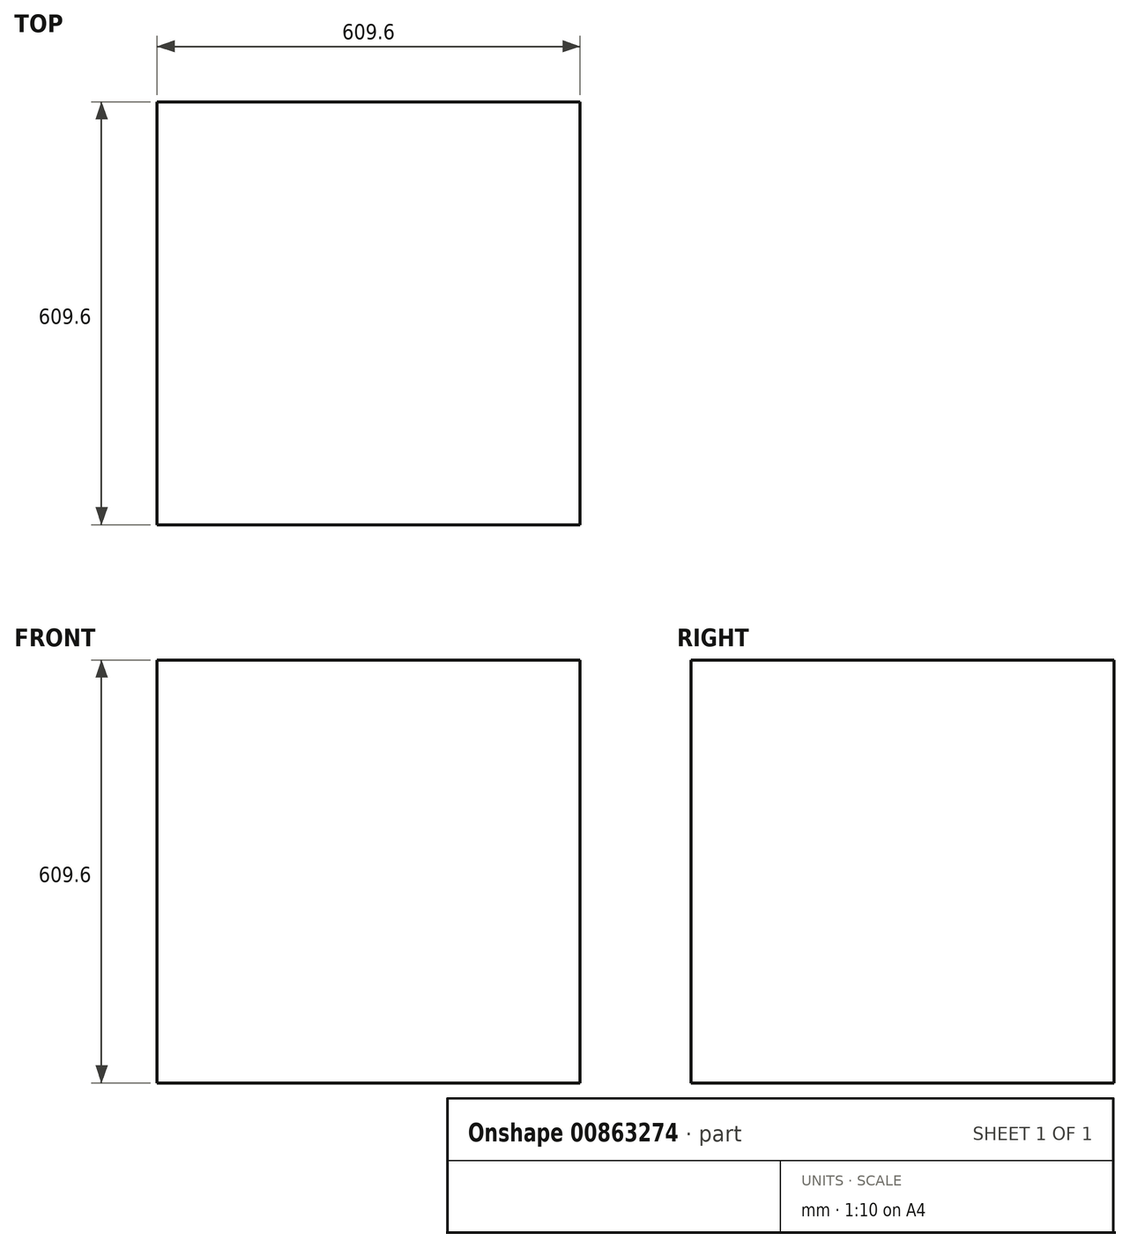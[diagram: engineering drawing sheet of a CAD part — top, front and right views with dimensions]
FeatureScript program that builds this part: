
annotation { "Feature Type Name" : "Feature", "Feature Type Description" : "" }
export const myFeature = defineFeature(function(context is Context, id is Id, definition is map)
    precondition{}
    {
        {
            var Q0;
            Q0=qCreatedBy(makeId("Front.planeOp"),FACE);
            var sketch = newSketch(context, id + "F0", { "sketchPlane" : qUnion([Q0])});
            skLineSegment(sketch, "E0.bottom", {"start": v(0, 0) * mm, "end": v(609.6, 0) * mm});
            skLineSegment(sketch, "E0.top", {"start": v(0, 609.6) * mm, "end": v(609.6, 609.6) * mm});
            skLineSegment(sketch, "E0.left", {"start": v(0, 0) * mm, "end": v(0, 609.6) * mm});
            skLineSegment(sketch, "E0.right", {"start": v(609.6, 0) * mm, "end": v(609.6, 609.6) * mm});
            skSolve(sketch);
        }
        {
            var Q0;
            Q0=makeQuery(id+"F0.imprint","IMPRINT",FACE,{"disambiguationData":[TD([[makeQuery(id+"F0.imprint","IMPRINT",EDGE,{"derivedFrom":sQuery(id+"F0.wireOp",EDGE,"E0.bottom")}),1.0]])]});
            extrude(context, id + "F1", {"entities" : qUnion([Q0]), "depth" : 609.6 * mm, "offsetDistance" : 30.48 * mm});
        }
    });
